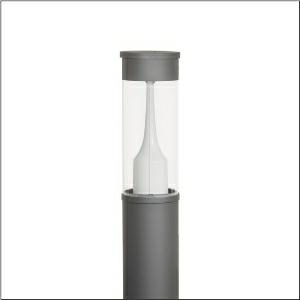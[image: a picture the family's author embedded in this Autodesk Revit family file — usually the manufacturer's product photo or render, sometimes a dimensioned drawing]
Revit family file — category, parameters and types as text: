
# Revit family: city-light_260_iq___p1_0a_5xa5295nf14h_1e18
name_source: partatom
category: Lighting Fixtures
units: mm (PartAtom-declared; Revit-internal decimal feet)

## family parameters
Cut with Voids When Loaded = No
Host = Face
Light Source = No
Part Type = Normal
Room Calculation Point = No
Round Connector Dimension = Use Diameter
Shared = No

## types (1)
- --- (1 x LED, 1510 lm, 11.8 W, 2700K)
    Apparent Load = 12 VA
    CIE Flux Codes = 32 61 90 93 100
    Color Rendering = 70
    Color Temperature = 2700K
    Default Elevation = 1800 mm
    Description = City-Light 260 iQ, light pillar, Module 540 iQ-SR, primary light control with 3 zone facetted reflector, of plastic, silver coated, highly specular, structured, primary optical cover: cover, of PMMA, transparent, partly coated, light distribution: P1.0a, primary light characteristic: strongly asymmetric, LED, High Power LED, rated luminous flux: 1.510lm, luminous efficacy: 128lm/W, light colour: 727, colour temperature: 2700K, control gear: ECG iQ, control: presetting dimming logarithmic, Street-Remote, Auto-Match, Temp-Guard, Lumen-Switch, Night-Set, Smart-Wire, Light-Fading, Desk-Remote (wireless, voltage-free reading and setting of iQ features in the workshop via application-optimized NFC function/RFID function), optimised constant luminous flux control (CLO 2.0), with terminal, 6-pole, max. 2.5mm², mains connection: 220..240V, AC, 50/60Hz, start of lifetime: 12W, end of lifetime: 12W, reduction: 6W, luminaire housing, cylindrical, of extruded aluminium section, coated, Siteco® metallic grey (DB 702S), length: 2.600mm, diameter: 200mm, Module 540 iQ-SR, traffic white (RAL 9016), equipment: standard, protection rating (complete): IP65, insulation class (complete): insulation class II (safety insulation), certification: CE, ENEC, VDE, packaging unit: 1 piece

Light Distribution: P1.0a
    Height = 500 mm
    Lamp = 1 x LED
    Lamp Light Flux = 1510 lm
    Lamp Power = 11.8 W
    Lamp count = 1
    Length = 200 mm  [stored 0.656168 ft]
    Luminous efficacy = 128 lm/W
    Manufacturer = Siteco
    ModVariant = No
    Model = 5XA5295NF14H
    Number of Poles = 1
    OnlyDefault = Yes
    Power Factor = 1
    Product Name = City-Light 260 iQ | P1.0a
    Product group = light pillar | pylon top
    ProductGroupID = 6103
    Protection Class = Protection class II
    Protection Degree = IP 65
    RLX_Detail_Level = 1
    RlxData = <blob elided: 52477 chars, md5=54534d00>
    Socket = socket
    Standby Power = 0 W
    System Light Flux = 1510 lm
    System Power = 12 W
    Type Comments = factory setting: luminous flux: 100 % | dim-lin: 254 | 472 mA
    Type Image = l_1006918.jpg
    URL = http://relux.com
    VarID = @adj_062993
    Voltage = 0 V
    Weight = 0.00 kg
    Width = 0 mm  [stored 0 ft]

note: [stored X ft] marks values corroborated as IEEE doubles in the binary element streams (Revit-internal decimal feet)

## geometry (parser evidence)
native form markers: Blend x4, Sweep x9
no freeform markers — native parametric forms only
